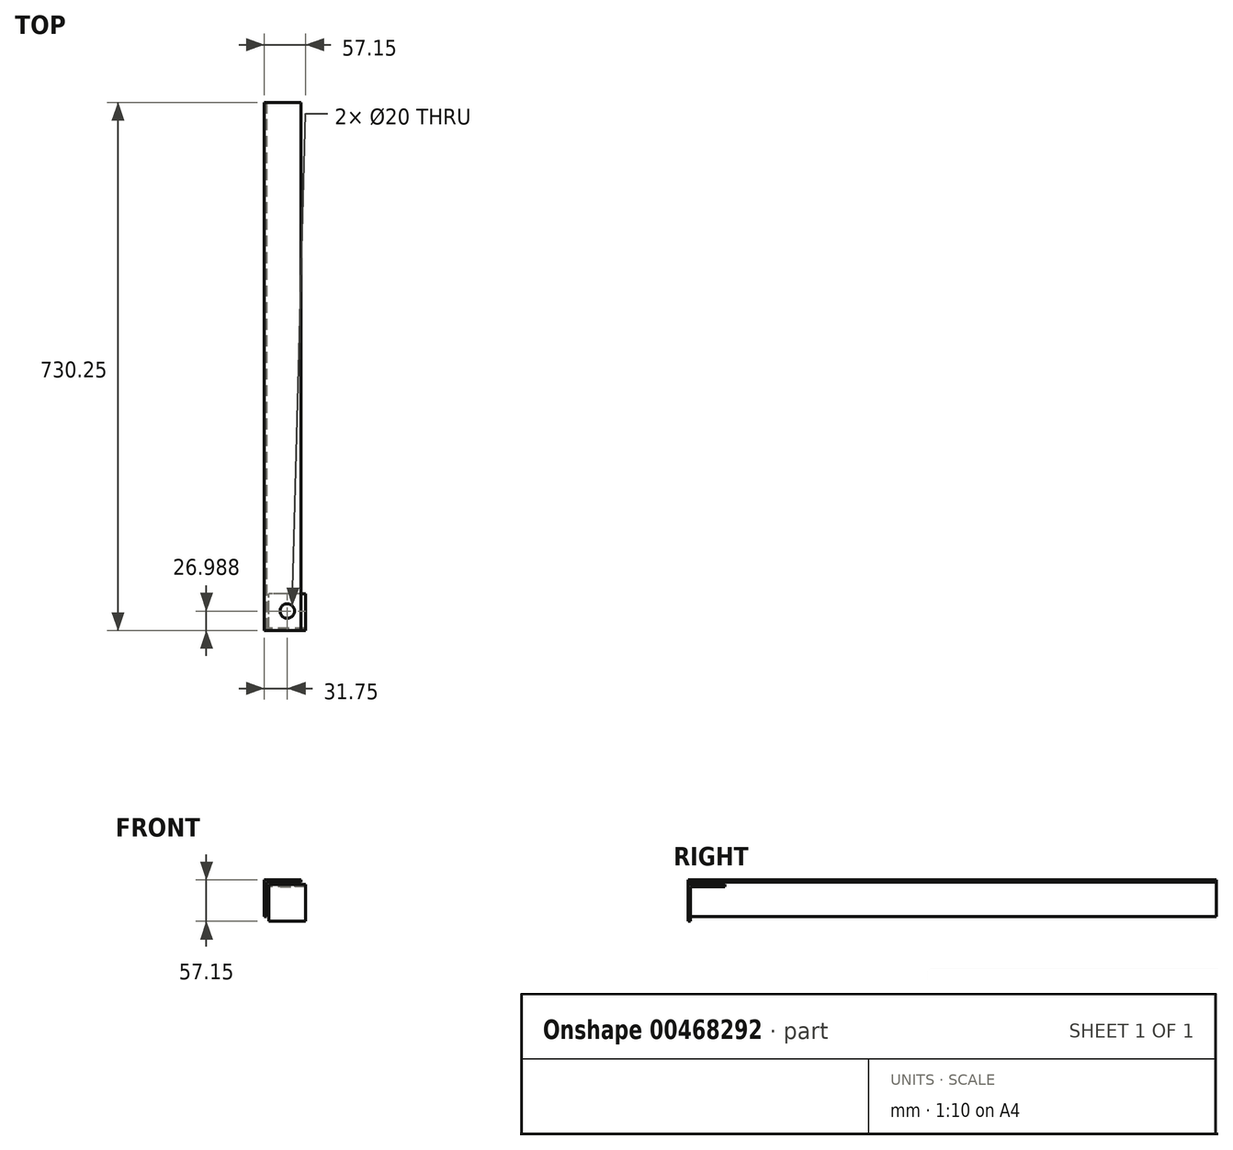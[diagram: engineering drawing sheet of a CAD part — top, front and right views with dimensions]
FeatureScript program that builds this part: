
annotation { "Feature Type Name" : "Feature", "Feature Type Description" : "" }
export const myFeature = defineFeature(function(context is Context, id is Id, definition is map)
    precondition{}
    {
        {
            var Q0;
            Q0=qCreatedBy(makeId("Right.planeOp"),FACE);
            var sketch = newSketch(context, id + "F0", { "sketchPlane" : qUnion([Q0])});
            skLineSegment(sketch, "E0.top", {"start": v(0, 50.8) * mm, "end": v(50.8, 50.8) * mm});
            skLineSegment(sketch, "E0.left", {"start": v(0, 0) * mm, "end": v(0, 50.8) * mm});
            skLineSegment(sketch, "E1.right", {"start": v(3.17, 0) * mm, "end": v(3.17, 47.63) * mm});
            skLineSegment(sketch, "E2", {"start": v(3.17, 0) * mm, "end": v(0, 0) * mm});
            skLineSegment(sketch, "E3", {"start": v(3.17, 47.63) * mm, "end": v(50.8, 47.63) * mm});
            skLineSegment(sketch, "E4", {"start": v(50.8, 47.63) * mm, "end": v(50.8, 50.8) * mm});
            skSolve(sketch);
        }
        {
            var Q0;
            Q0=qSketchRegion(id+"F0",true);
            extrude(context, id + "F1", {"entities" : qUnion([Q0]), "depth" : 50.8 * mm});
        }
        {
            var Q0;
            Q0=qCreatedBy(makeId("Front.planeOp"),FACE);
            var sketch = newSketch(context, id + "F2", { "sketchPlane" : qUnion([Q0])});
            skLineSegment(sketch, "E5.top", {"start": v(-6.35, 57.15) * mm, "end": v(44.45, 57.15) * mm});
            skLineSegment(sketch, "E5.left", {"start": v(-6.35, 6.35) * mm, "end": v(-6.35, 57.15) * mm});
            skLineSegment(sketch, "E6.right", {"start": v(-3.18, 6.35) * mm, "end": v(-3.18, 53.98) * mm});
            skLineSegment(sketch, "E7", {"start": v(-3.18, 6.35) * mm, "end": v(-6.35, 6.35) * mm});
            skLineSegment(sketch, "E8", {"start": v(-3.17, 53.98) * mm, "end": v(44.45, 53.98) * mm});
            skLineSegment(sketch, "E9", {"start": v(44.45, 53.98) * mm, "end": v(44.45, 57.15) * mm});
            skSolve(sketch);
        }
        {
            var Q0;
            Q0=qSketchRegion(id+"F2",true);
            extrude(context, id + "F3", {"entities" : qUnion([Q0]), "oppositeDirection" : true, "depth" : 730.25 * mm});
        }
        {
            var Q0;
            Q0=makeQuery(id+"F1.opExtrude","SWEPT_FACE",FACE,{"disambiguationData":[OSD([sQuery(id+"F0.wireOp",EDGE,"E3")])]});
            var sketch = newSketch(context, id + "F4", { "sketchPlane" : qUnion([Q0])});
            skCircle(sketch, "E10", {"center": v(25.4, -26.99) * mm, "radius": 10 * mm});
            skPoint(sketch, "E10.centerSnap0", {"position": v(25.4, -50.8) * mm});
            skPoint(sketch, "E10.centerSnap1", {"position": v(0, -26.99) * mm});
            skSolve(sketch);
        }
        {
            var Q0;
            Q0=qSketchRegion(id+"F4",true);
            extrude(context, id + "F5", {"entities" : qUnion([Q0]), "operationType" : NewBodyOperationType.REMOVE, "endBound" : BoundingType.THROUGH_ALL, "oppositeDirection" : true, "depth" : 25.4 * mm});
        }
        {
            var Q0;
            Q0=makeQuery(id+"F3.opExtrude","CAP_FACE",FACE,{"disambiguationData":[OSD([sQuery(id+"F2.wireOp",EDGE,"E5.top"),sQuery(id+"F2.wireOp",EDGE,"E5.left"),sQuery(id+"F2.wireOp",EDGE,"E6.right"),sQuery(id+"F2.wireOp",EDGE,"E7"),sQuery(id+"F2.wireOp",EDGE,"E8"),sQuery(id+"F2.wireOp",EDGE,"E9")])],"isStart":true});
            var Q1;
            Q1=makeQuery(id+"F3.opExtrude","CAP_FACE",FACE,{"disambiguationData":[OSD([sQuery(id+"F2.wireOp",EDGE,"E5.top"),sQuery(id+"F2.wireOp",EDGE,"E5.left"),sQuery(id+"F2.wireOp",EDGE,"E6.right"),sQuery(id+"F2.wireOp",EDGE,"E7"),sQuery(id+"F2.wireOp",EDGE,"E8"),sQuery(id+"F2.wireOp",EDGE,"E9")])],"isStart":false});
            cPlane(context, id + "F6", {"entities" : qUnion([Q0, Q1]), "cplaneType" : CPlaneType.MID_PLANE, "offset" : 25.4 * mm, "width" : 152.4 * mm, "height" : 152.4 * mm});
        }
    });
